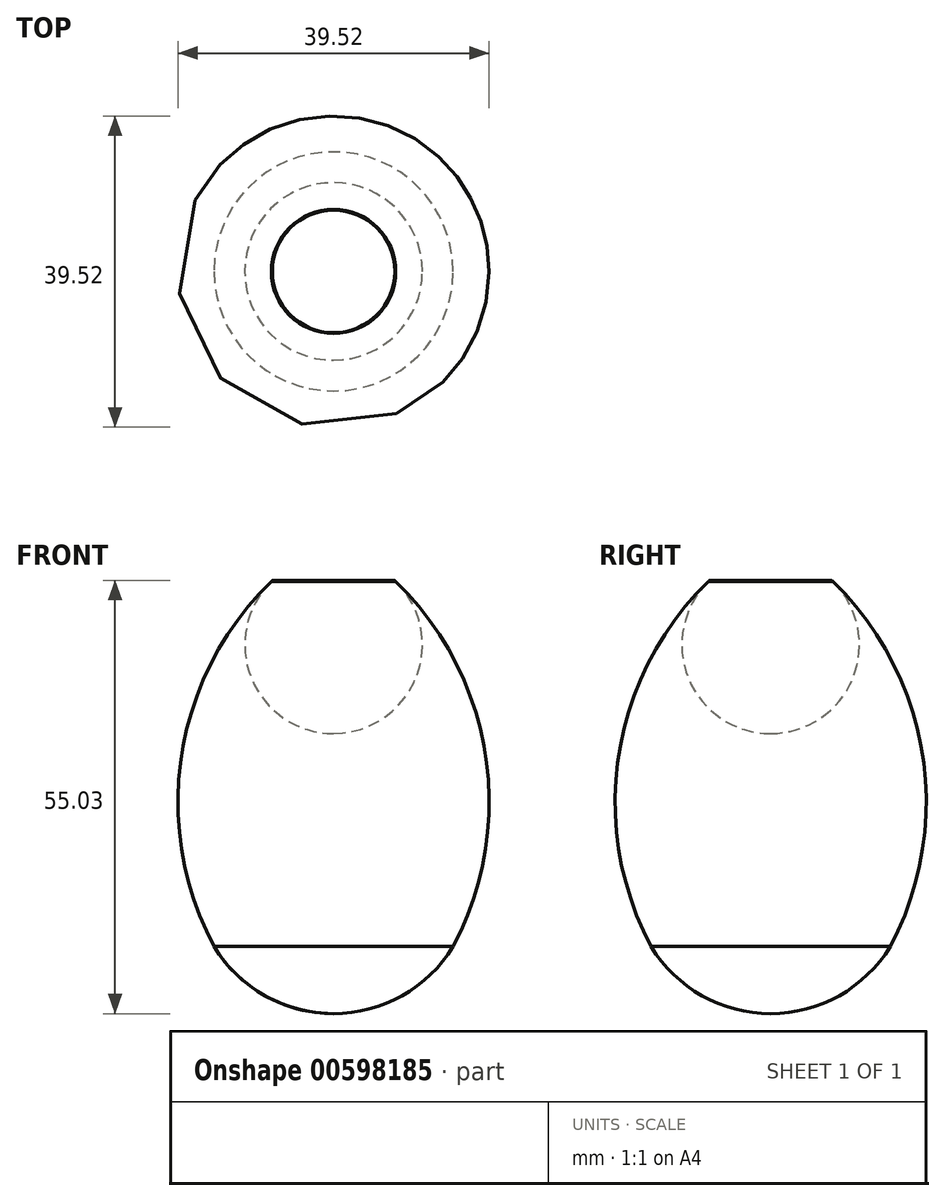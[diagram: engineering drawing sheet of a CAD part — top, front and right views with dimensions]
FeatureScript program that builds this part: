
annotation { "Feature Type Name" : "Feature", "Feature Type Description" : "" }
export const myFeature = defineFeature(function(context is Context, id is Id, definition is map)
    precondition{}
    {
        {
            var Q0;
            Q0=qCreatedBy(makeId("Front.planeOp"),FACE);
            var sketch = newSketch(context, id + "F0", { "sketchPlane" : qUnion([Q0])});
            skCircle(sketch, "E0", {"center": v(0, -17.8) * mm, "radius": 17.8 * mm});
            skCircle(sketch, "E1", {"center": v(0, 11.28) * mm, "radius": 11.28 * mm});
            skArc(sketch, "E2", {"start": v(-7.78, 19.44) * mm, "mid": v(-19.22, -2.58) * mm, "end": v(-15.19, -27.06) * mm});
            skArc(sketch, "E3", {"start": v(15.19, -27.06) * mm, "mid": v(19.28, -2.57) * mm, "end": v(7.78, 19.44) * mm});
            skLineSegment(sketch, "E4", {"start": v(0, 22.55) * mm, "end": v(0, -25.48) * mm});
            skLineSegment(sketch, "E5", {"start": v(0, -25.48) * mm, "end": v(0, -35.59) * mm});
            skSolve(sketch);
        }
        {
            var Q0;
            {var subQ0=sQuery(id+"F0.wireOp",EDGE,"E3");var subQ3=sQuery(id+"F0.wireOp",EDGE,"E1");var subQ5=makeQuery(id+"F0.imprint","INTERSECT",VERTEX,{"derivedFrom":[subQ3,subQ0]});Q0=makeQuery(id+"F0.imprint","IMPRINT",FACE,{"disambiguationData":[TD([[makeQuery(id+"F0.imprint","IMPRINT",EDGE,{"disambiguationData":[TD([[subQ5,1.0]])],"derivedFrom":subQ0}),1.0]])]});}
            var Q1;
            {var subQ0=sQuery(id+"F0.wireOp",EDGE,"E1");var subQ1=makeQuery(id+"F0.imprint","INTERSECT",VERTEX,{"derivedFrom":[subQ0,sQuery(id+"F0.wireOp",EDGE,"E3")]});Q1=makeQuery(id+"F0.imprint","IMPRINT",FACE,{"disambiguationData":[TD([[makeQuery(id+"F0.imprint","IMPRINT",EDGE,{"disambiguationData":[TD([[subQ1,-1.0]])],"derivedFrom":subQ0}),1.0]])]});}
            var Q2;
            {var subQ0=sQuery(id+"F0.wireOp",EDGE,"E5");Q2=makeQuery(id+"F0.imprint","IMPRINT",FACE,{"disambiguationData":[TD([[makeQuery(id+"F0.imprint","IMPRINT",EDGE,{"derivedFrom":subQ0}),1.0]])]});}
            var Q3;
            Q3=sQuery(id+"F0.wireOp",EDGE,"E4");
            revolve(context, id + "F1", {"entities" : qUnion([Q0, Q1, Q2]), "axis" : qUnion([Q3]), "revolveType" : RevolveType.FULL});
        }
    });
